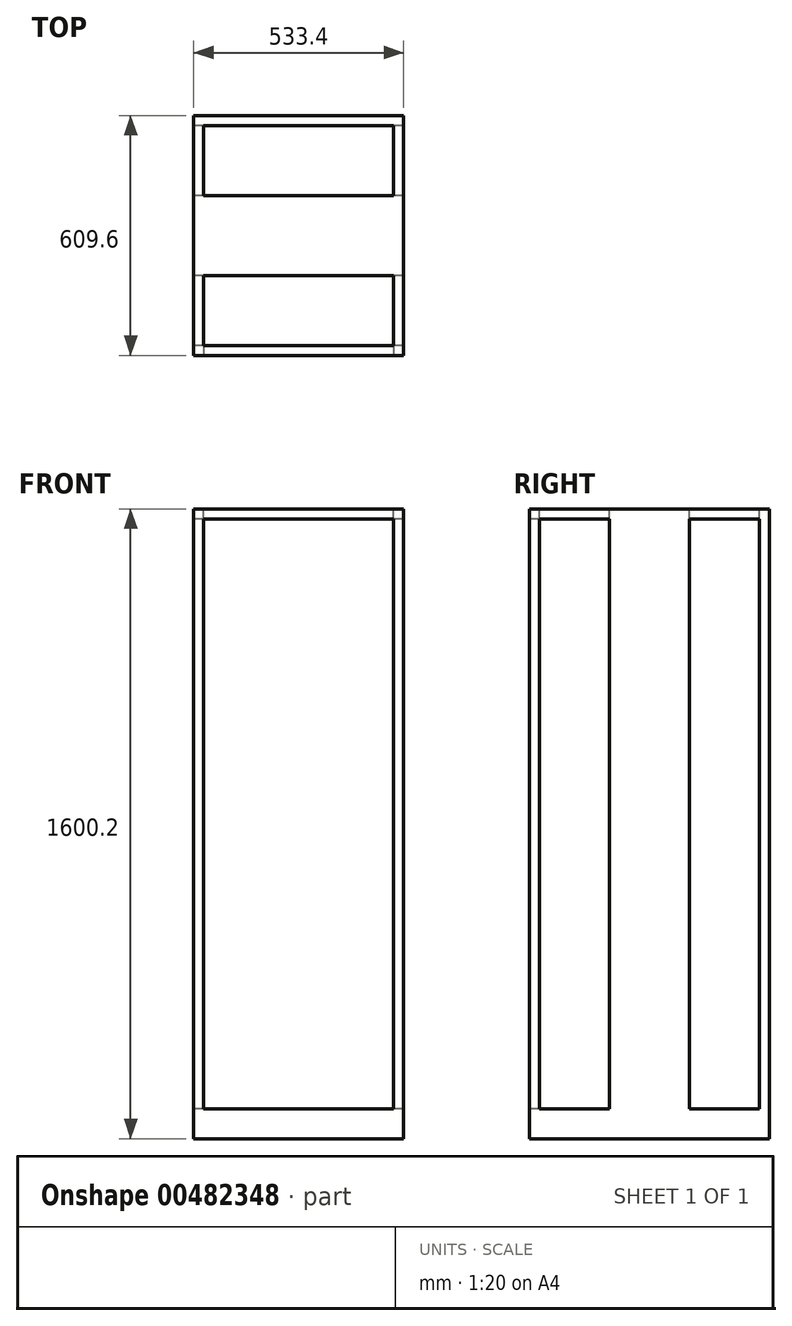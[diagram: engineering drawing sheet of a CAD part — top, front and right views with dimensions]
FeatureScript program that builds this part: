
annotation { "Feature Type Name" : "Feature", "Feature Type Description" : "" }
export const myFeature = defineFeature(function(context is Context, id is Id, definition is map)
    precondition{}
    {
        {
            var Q0;
            Q0=qCreatedBy(makeId("Top.planeOp"),FACE);
            var sketch = newSketch(context, id + "F0", { "sketchPlane" : qUnion([Q0])});
            skLineSegment(sketch, "E0.bottom", {"start": v(0, 0) * mm, "end": v(533.4, 0) * mm});
            skLineSegment(sketch, "E0.top", {"start": v(0, 609.6) * mm, "end": v(533.4, 609.6) * mm});
            skLineSegment(sketch, "E0.left", {"start": v(0, 0) * mm, "end": v(0, 609.6) * mm});
            skLineSegment(sketch, "E0.right", {"start": v(533.4, 0) * mm, "end": v(533.4, 609.6) * mm});
            skLineSegment(sketch, "E1.bottom", {"start": v(0, 406.4) * mm, "end": v(533.4, 406.4) * mm});
            skLineSegment(sketch, "E1.top", {"start": v(0, 203.2) * mm, "end": v(533.4, 203.2) * mm});
            skLineSegment(sketch, "E1.left", {"start": v(0, 203.2) * mm, "end": v(0, 406.4) * mm});
            skLineSegment(sketch, "E1.right", {"start": v(533.4, 203.2) * mm, "end": v(533.4, 406.4) * mm});
            skPoint(sketch, "E2", {"position": v(0, 304.8) * mm});
            skSolve(sketch);
        }
        {
            var Q0;
            {var subQ0=sQuery(id+"F0.wireOp",EDGE,"E0.top");Q0=makeQuery(id+"F0.imprint","IMPRINT",FACE,{"disambiguationData":[TD([[makeQuery(id+"F0.imprint","IMPRINT",EDGE,{"derivedFrom":subQ0}),-1.0]])]});}
            var Q1;
            {var subQ0=sQuery(id+"F0.wireOp",EDGE,"E0.bottom");Q1=makeQuery(id+"F0.imprint","IMPRINT",FACE,{"disambiguationData":[TD([[makeQuery(id+"F0.imprint","IMPRINT",EDGE,{"derivedFrom":subQ0}),1.0]])]});}
            var Q2;
            Q2=makeQuery(id+"F0.imprint","IMPRINT",FACE,{"disambiguationData":[TD([[makeQuery(id+"F0.imprint","IMPRINT",EDGE,{"derivedFrom":sQuery(id+"F0.wireOp",EDGE,"E1.bottom")}),-1.0]])]});
            extrude(context, id + "F1", {"entities" : qUnion([Q0, Q1, Q2]), "depth" : 1600.2 * mm, "offsetDistance" : 25.4 * mm});
        }
        {
            var Q0;
            Q0=makeQuery(id+"F1.opExtrude","SWEPT_FACE",FACE,{"disambiguationData":[OSD([sQuery(id+"F0.wireOp",EDGE,"E0.left"),sQuery(id+"F0.wireOp",EDGE,"E1.left")])]});
            var sketch = newSketch(context, id + "F2", { "sketchPlane" : qUnion([Q0])});
            skLineSegment(sketch, "E3.bottom", {"start": v(-584.2, 1574.8) * mm, "end": v(-406.4, 1574.8) * mm});
            skLineSegment(sketch, "E3.top", {"start": v(-584.2, 76.2) * mm, "end": v(-406.4, 76.2) * mm});
            skLineSegment(sketch, "E3.left", {"start": v(-584.2, 1574.8) * mm, "end": v(-584.2, 76.2) * mm});
            skLineSegment(sketch, "E3.right", {"start": v(-406.4, 1574.8) * mm, "end": v(-406.4, 76.2) * mm});
            skLineSegment(sketch, "E4", {"start": v(-304.8, 1600.2) * mm, "end": v(-304.8, 1786.1) * mm, "construction": true});
            skLineSegment(sketch, "E5.MirrorCS", {"start": v(-203.2, 1574.8) * mm, "end": v(-203.2, 76.2) * mm});
            skLineSegment(sketch, "E6.MirrorCS", {"start": v(-25.4, 1574.8) * mm, "end": v(-25.4, 76.2) * mm});
            skLineSegment(sketch, "E7.MirrorCS", {"start": v(-25.4, 1574.8) * mm, "end": v(-203.2, 1574.8) * mm});
            skLineSegment(sketch, "E8.MirrorCS", {"start": v(-25.4, 76.2) * mm, "end": v(-203.2, 76.2) * mm});
            skSolve(sketch);
        }
        {
            var Q0;
            Q0 = qSketchRegion(id + "F2", true);
            extrude(context, id + "F3", {"entities" : qUnion([Q0]), "operationType" : NewBodyOperationType.REMOVE, "endBound" : BoundingType.THROUGH_ALL, "oppositeDirection" : true, "depth" : 25.4 * mm, "offsetDistance" : 25.4 * mm});
        }
        {
            var Q0;
            Q0=makeQuery(id+"F1.opExtrude","CAP_FACE",FACE,{"disambiguationData":[OSD([sQuery(id+"F0.wireOp",EDGE,"E0.bottom"),sQuery(id+"F0.wireOp",EDGE,"E0.top"),sQuery(id+"F0.wireOp",EDGE,"E0.left"),sQuery(id+"F0.wireOp",EDGE,"E0.right"),sQuery(id+"F0.wireOp",EDGE,"E1.left"),sQuery(id+"F0.wireOp",EDGE,"E1.right")])],"isStart":false});
            var sketch = newSketch(context, id + "F4", { "sketchPlane" : qUnion([Q0])});
            skLineSegment(sketch, "E9.bottom", {"start": v(25.4, 406.4) * mm, "end": v(508, 406.4) * mm});
            skLineSegment(sketch, "E9.top", {"start": v(25.4, 584.2) * mm, "end": v(508, 584.2) * mm});
            skLineSegment(sketch, "E9.left", {"start": v(25.4, 406.4) * mm, "end": v(25.4, 584.2) * mm});
            skLineSegment(sketch, "E9.right", {"start": v(508, 406.4) * mm, "end": v(508, 584.2) * mm});
            skLineSegment(sketch, "E10.bottom", {"start": v(25.4, 203.2) * mm, "end": v(508, 203.2) * mm});
            skLineSegment(sketch, "E10.top", {"start": v(25.4, 25.4) * mm, "end": v(508, 25.4) * mm});
            skLineSegment(sketch, "E10.left", {"start": v(25.4, 203.2) * mm, "end": v(25.4, 25.4) * mm});
            skLineSegment(sketch, "E10.right", {"start": v(508, 203.2) * mm, "end": v(508, 25.4) * mm});
            skSolve(sketch);
        }
        {
            var Q0;
            Q0 = qSketchRegion(id + "F4", true);
            extrude(context, id + "F5", {"entities" : qUnion([Q0]), "operationType" : NewBodyOperationType.REMOVE, "oppositeDirection" : true, "depth" : 76.2 * mm, "offsetDistance" : 25.4 * mm});
        }
        {
            var Q0;
            Q0=makeQuery(id+"F1.opExtrude","SWEPT_FACE",FACE,{"disambiguationData":[OSD([sQuery(id+"F0.wireOp",EDGE,"E0.bottom")])]});
            var sketch = newSketch(context, id + "F6", { "sketchPlane" : qUnion([Q0])});
            skLineSegment(sketch, "E11.bottom", {"start": v(25.4, 1574.8) * mm, "end": v(508, 1574.8) * mm});
            skLineSegment(sketch, "E11.top", {"start": v(25.4, 76.2) * mm, "end": v(508, 76.2) * mm});
            skLineSegment(sketch, "E11.left", {"start": v(25.4, 1574.8) * mm, "end": v(25.4, 76.2) * mm});
            skLineSegment(sketch, "E11.right", {"start": v(508, 1574.8) * mm, "end": v(508, 76.2) * mm});
            skSolve(sketch);
        }
        {
            var Q0;
            Q0 = qSketchRegion(id + "F6", true);
            extrude(context, id + "F7", {"entities" : qUnion([Q0]), "operationType" : NewBodyOperationType.REMOVE, "oppositeDirection" : true, "depth" : 50.8 * mm, "offsetDistance" : 25.4 * mm});
        }
        {
            var Q0;
            Q0=makeQuery(id+"F5.boolean.opBoolean","MERGE",FACE,{"derivedFrom":[makeQuery(id+"F3.boolean.opBoolean","COPY",FACE,{"derivedFrom":makeQuery(id+"F3.opExtrude","SWEPT_FACE",FACE,{"disambiguationData":[OSD([sQuery(id+"F2.wireOp",EDGE,"E5.MirrorCS")])]})}),makeQuery(id+"F5.opExtrude","SWEPT_FACE",FACE,{"disambiguationData":[OSD([sQuery(id+"F4.wireOp",EDGE,"E10.bottom")])]})]});
            var Q1;
            Q1=makeQuery(id+"F5.boolean.opBoolean","MERGE",FACE,{"derivedFrom":[makeQuery(id+"F3.boolean.opBoolean","COPY",FACE,{"derivedFrom":makeQuery(id+"F3.opExtrude","SWEPT_FACE",FACE,{"disambiguationData":[OSD([sQuery(id+"F2.wireOp",EDGE,"E3.right")])]})}),makeQuery(id+"F5.opExtrude","SWEPT_FACE",FACE,{"disambiguationData":[OSD([sQuery(id+"F4.wireOp",EDGE,"E9.bottom")])]})]});
            cPlane(context, id + "F8", {"entities" : qUnion([Q0, Q1]), "cplaneType" : CPlaneType.MID_PLANE, "offset" : 25.4 * mm, "width" : 152.4 * mm, "height" : 152.4 * mm});
        }
    });
